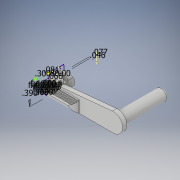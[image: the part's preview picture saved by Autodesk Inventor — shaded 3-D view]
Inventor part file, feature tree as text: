
AUTODESK INVENTOR PART (.ipt)
format: ipt  version: 2018.3 (Build 223284000, 284)  size: 260,096 bytes
history: native  units: in
note: dims shown in document units (in); Inventor stores cm internally (conversion verified against a paired STEP export)
features: extrude x7, sketch x3, fillet x2, revolve x1, plane x1, chamfer x1
ambient origin geometry x8: Origin, YZ Plane, XZ Plane, XY Plane, X Axis, Y Axis, Z Axis, Center Point
bodies: Solid1 (feature_tree)
feature tree (15):
  sketch  "Sketch1"  dims[d0=0.2005in d1=0.99in]
  extrude  "Extrusion1"  Depth=0.99in
  extrude  "Extrusion2"  Depth=0.344in
  revolve  "Revolution1"  [1 undecoded]
  fillet  "Fillet1"  Radius=0.256in
  extrude  "Extrusion3"  Depth=0.01in
  extrude  "Extrusion4"  Depth=0.01in
  plane  "Work Plane1"
  sketch  "Sketch3"  dims[d4=0.0206in d5=0.2in d6=0.256in d7=0.042in d8=1.0875in d9=1.1991in d10=0.081in d11=0.0in d12=0.867in d13=0.0in d14=0.22in d15=90.0deg d16=0.03in d17=0.115in d18=0.0in d19=0.198in d20=0.0in d21=0.0in d30=0.39in d31=0.6in d32=0.18in d33=0.4in d35=60.0deg d37=0.046in d38=0.4895in d39=0.0in d40=0.081in d41=0.066in d42=0.077in d43=60.0deg d45=60.0deg d46=0.015in d47=60.0deg d48=0.015in d49=60.0deg d50=0.015in d51=0.027in d52=0.027in d53=0.027in d54=0.3645in d55=0.0in d56=0.2in d57=0.2998in d58=0.2998in d59=0.2998in d60=0.2998in d61=0.017in d62=0.017in d63=0.017in d64=0.017in d65=0.3in d66=0.016in d67=0.016in d68=0.016in d69=0.016in d70=0.0178in d71=0.46in d72=0.0in d73=0.105in d74=0.125in d75=45.0deg d76=0.01in]
  extrude  "Extrusion7"  Depth=0.01in
  extrude  "Extrusion8"  Depth=0.01in TaperAngle=0.0deg
  extrude  "Extrusion9"  Depth=0.01in TaperAngle=0.0deg
  chamfer  "Chamfer2"  Distance=0.22in
  fillet  "Fillet2"  [1 undecoded]
  sketch  "Sketch2"  dims[d2=1.194in d3=0.344in]
note: 2 required parameter values undecoded (feature->parameter linkage not recoverable at this tier; creation-order binding heuristic only, values carry confidence <= 0.55)